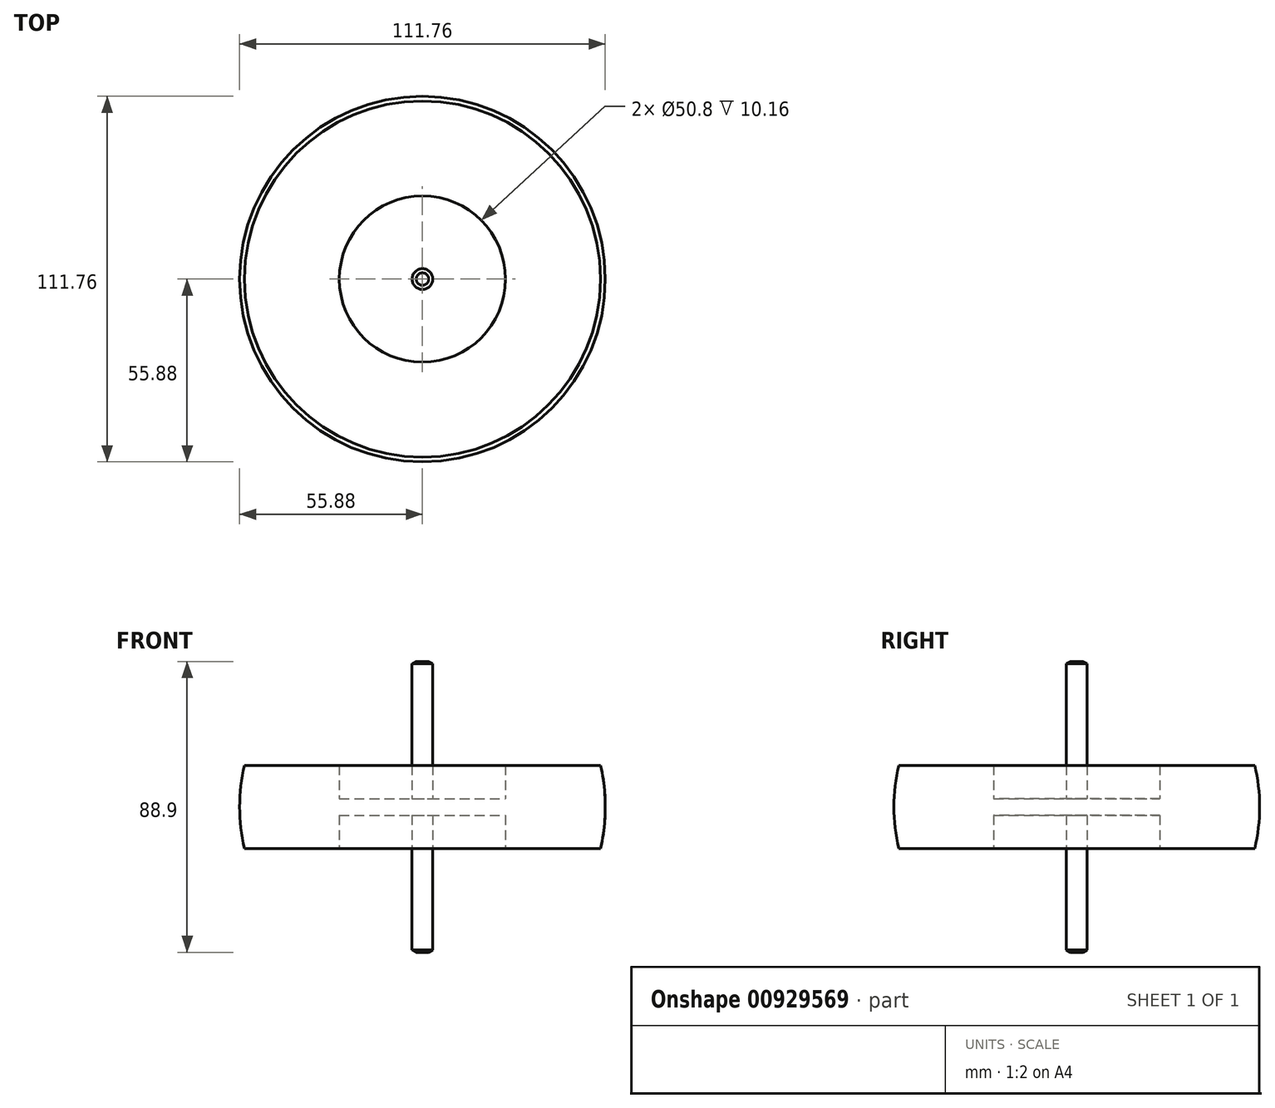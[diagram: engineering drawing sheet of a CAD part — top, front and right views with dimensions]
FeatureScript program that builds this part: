
annotation { "Feature Type Name" : "Feature", "Feature Type Description" : "" }
export const myFeature = defineFeature(function(context is Context, id is Id, definition is map)
    precondition{}
    {
        {
            var Q0;
            Q0=qCreatedBy(makeId("Front.planeOp"),FACE);
            var sketch = newSketch(context, id + "F0", { "sketchPlane" : qUnion([Q0])});
            skLineSegment(sketch, "E0", {"start": v(0, 0) * mm, "end": v(0, 44.45) * mm, "construction": true});
            skLineSegment(sketch, "E1", {"start": v(0, 44.45) * mm, "end": v(0, 44.45) * mm});
            skLineSegment(sketch, "E2", {"start": v(0, 44.45) * mm, "end": v(3.17, 44.45) * mm});
            skLineSegment(sketch, "E3", {"start": v(3.17, 44.45) * mm, "end": v(3.17, 2.54) * mm});
            skLineSegment(sketch, "E4", {"start": v(3.18, 2.54) * mm, "end": v(25.4, 2.54) * mm});
            skLineSegment(sketch, "E5", {"start": v(25.4, 2.54) * mm, "end": v(25.4, 12.7) * mm});
            skLineSegment(sketch, "E6", {"start": v(25.4, 12.7) * mm, "end": v(25.48, 12.7) * mm});
            skLineSegment(sketch, "E7", {"start": v(25.48, 12.7) * mm, "end": v(25.48, 12.7) * mm});
            skLineSegment(sketch, "E8", {"start": v(25.4, 12.7) * mm, "end": v(50.8, 12.7) * mm});
            skLineSegment(sketch, "E9", {"start": v(50.8, 12.7) * mm, "end": v(50.8, 0) * mm});
            skLineSegment(sketch, "E10", {"start": v(0, 0) * mm, "end": v(50.8, 0) * mm});
            skLineSegment(sketch, "E11.MirrorCS", {"start": v(25.4, -12.7) * mm, "end": v(50.8, -12.7) * mm});
            skLineSegment(sketch, "E12.MirrorCS", {"start": v(50.8, -12.7) * mm, "end": v(50.8, 0) * mm});
            skLineSegment(sketch, "E13.MirrorCS", {"start": v(25.4, -2.54) * mm, "end": v(25.4, -12.7) * mm});
            skLineSegment(sketch, "E14.MirrorCS", {"start": v(3.18, -2.54) * mm, "end": v(25.4, -2.54) * mm});
            skLineSegment(sketch, "E15.MirrorCS", {"start": v(3.18, -44.45) * mm, "end": v(3.17, -2.54) * mm});
            skLineSegment(sketch, "E16.MirrorCS", {"start": v(0, 0) * mm, "end": v(0, -44.45) * mm, "construction": true});
            skLineSegment(sketch, "E17.MirrorCS", {"start": v(0, -44.45) * mm, "end": v(3.18, -44.45) * mm});
            skLineSegment(sketch, "E18", {"start": v(0, -44.45) * mm, "end": v(0, 44.45) * mm});
            skSolve(sketch);
        }
        {
            var Q0;
            {var subQ2=sQuery(id+"F0.wireOp",EDGE,"E2");Q0=makeQuery(id+"F0.imprint","IMPRINT",FACE,{"disambiguationData":[TD([[makeQuery(id+"F0.imprint","IMPRINT",EDGE,{"derivedFrom":subQ2}),-1.0]])]});}
            var Q1;
            {var subQ0=sQuery(id+"F0.wireOp",EDGE,"E10");Q1=makeQuery(id+"F0.imprint","IMPRINT",FACE,{"disambiguationData":[TD([[makeQuery(id+"F0.imprint","IMPRINT",EDGE,{"derivedFrom":subQ0}),-1.0]])]});}
            var Q2;
            Q2=sQuery(id+"F0.wireOp",EDGE,"E18");
            revolve(context, id + "F1", {"surfaceOperationType" : NewSurfaceOperationType.NEW, "entities" : qUnion([Q0, Q1]), "axis" : qUnion([Q2]), "revolveType" : RevolveType.FULL});
        }
        {
            var Q0;
            Q0=makeQuery(id+"F1.opRevolve","SWEPT_EDGE",EDGE,{"disambiguationData":[OSD([sQuery(id+"F0.wireOp",EDGE,"E2"),sQuery(id+"F0.wireOp",EDGE,"E3")])]});
            chamfer(context, id + "F2", {"entities" : qUnion([Q0]), "chamferType" : ChamferType.OFFSET_ANGLE, "width" : 5.08 * mm, "oppositeDirection" : false, "angle" : 30 * degree, "tangentPropagation" : true});
        }
        {
            var Q0;
            Q0=makeQuery(id+"F1.opRevolve","SWEPT_EDGE",EDGE,{"disambiguationData":[OSD([sQuery(id+"F0.wireOp",EDGE,"E15.MirrorCS"),sQuery(id+"F0.wireOp",EDGE,"E17.MirrorCS")])]});
            chamfer(context, id + "F3", {"entities" : qUnion([Q0]), "chamferType" : ChamferType.OFFSET_ANGLE, "width" : 5.08 * mm, "oppositeDirection" : true, "angle" : 30 * degree, "tangentPropagation" : true});
        }
        {
            var Q0;
            Q0=qCreatedBy(makeId("Front.planeOp"),FACE);
            var sketch = newSketch(context, id + "F4", { "sketchPlane" : qUnion([Q0])});
            skArc(sketch, "E19", {"start": v(54.42, -12.7) * mm, "mid": v(55.88, 0) * mm, "end": v(54.42, 12.7) * mm});
            skLineSegment(sketch, "E20.0", {"start": v(50.8, 12.7) * mm, "end": v(-50.8, 12.7) * mm});
            skLineSegment(sketch, "E21", {"start": v(-50.8, -12.7) * mm, "end": v(-50.8, 12.7) * mm});
            skLineSegment(sketch, "E22", {"start": v(50.8, 12.7) * mm, "end": v(50.8, -12.7) * mm});
            skLineSegment(sketch, "E23.0", {"start": v(50.8, -12.7) * mm, "end": v(-50.8, -12.7) * mm});
            skLineSegment(sketch, "E24", {"start": v(50.8, -12.7) * mm, "end": v(54.42, -12.7) * mm});
            skLineSegment(sketch, "E25", {"start": v(50.8, 12.7) * mm, "end": v(54.42, 12.7) * mm});
            skSolve(sketch);
        }
        {
            var Q0;
            Q0=makeQuery(id+"F4.imprint","IMPRINT",FACE,{"disambiguationData":[TD([[makeQuery(id+"F4.imprint","IMPRINT",EDGE,{"derivedFrom":sQuery(id+"F4.wireOp",EDGE,"E19")}),1.0]])]});
            var Q1;
            Q1=makeQuery(id+"F1.opRevolve","SWEPT_EDGE",EDGE,{"disambiguationData":[OSD([sQuery(id+"F0.wireOp",EDGE,"E8"),sQuery(id+"F0.wireOp",EDGE,"E9")])]});
            revolve(context, id + "F5", {"operationType" : NewBodyOperationType.ADD, "surfaceOperationType" : NewSurfaceOperationType.NEW, "entities" : qUnion([Q0]), "axis" : qUnion([Q1]), "revolveType" : RevolveType.FULL});
        }
    });
